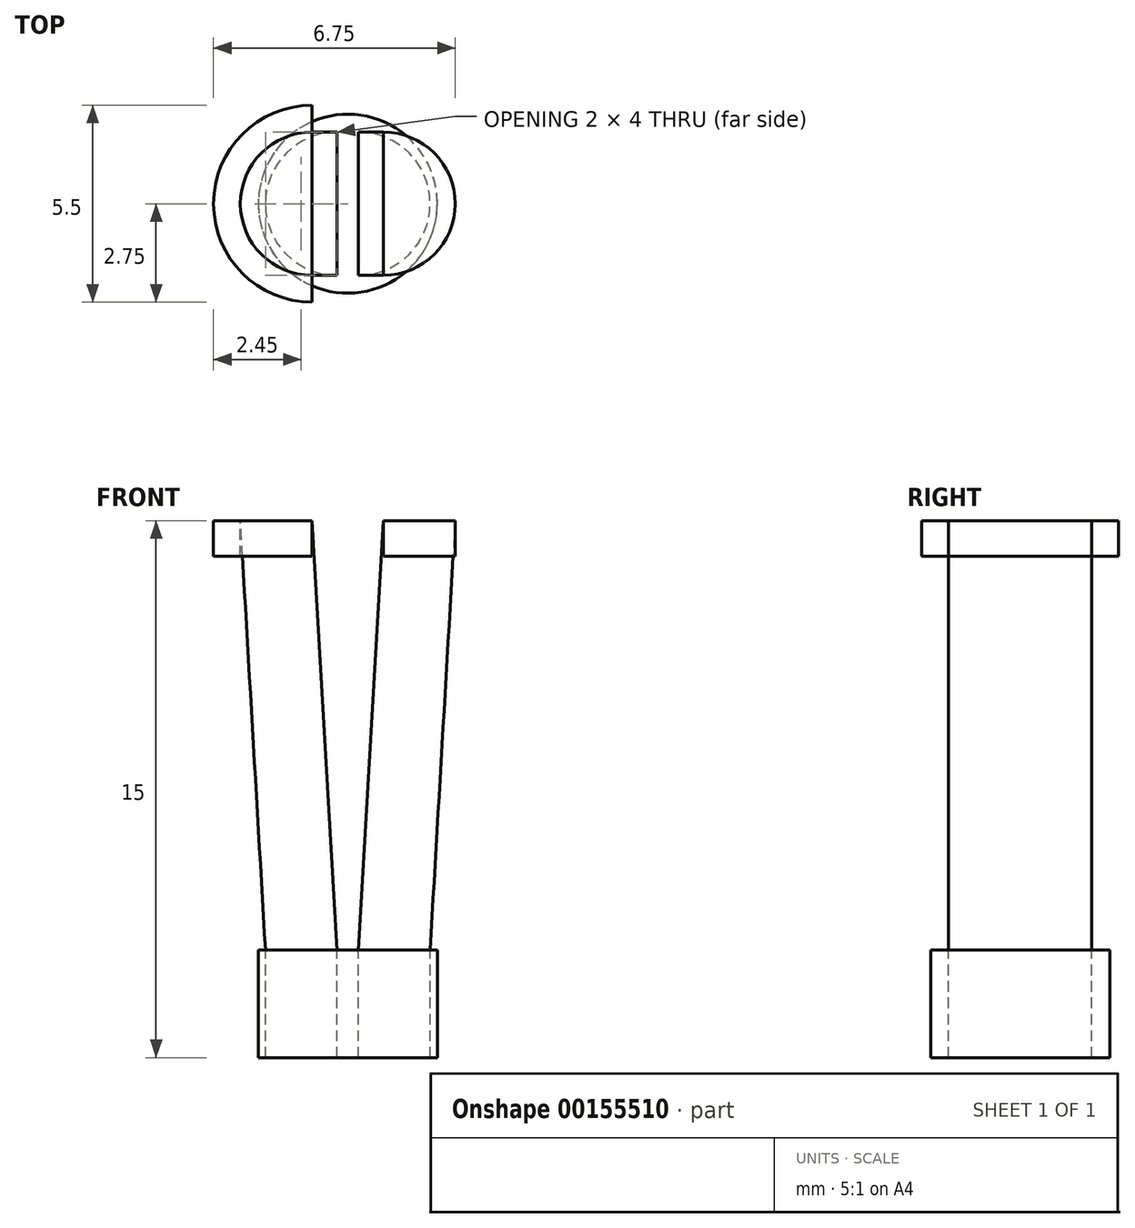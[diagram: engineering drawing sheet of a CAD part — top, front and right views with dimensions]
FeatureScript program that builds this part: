
annotation { "Feature Type Name" : "Feature", "Feature Type Description" : "" }
export const myFeature = defineFeature(function(context is Context, id is Id, definition is map)
    precondition{}
    {
        {
            var Q0;
            Q0=qCreatedBy(makeId("Top.planeOp"),FACE);
            cPlane(context, id + "F0", {"entities" : qUnion([Q0]), "cplaneType" : CPlaneType.OFFSET, "offset" : 6 * mm, "width" : 150 * mm, "height" : 150 * mm});
        }
        {
            var Q0;
            Q0=qCreatedBy(makeId("Top.planeOp"),FACE);
            cPlane(context, id + "F1", {"entities" : qUnion([Q0]), "cplaneType" : CPlaneType.OFFSET, "offset" : 6 * mm, "oppositeDirection" : true, "width" : 150 * mm, "height" : 150 * mm});
        }
        {
            var Q0;
            Q0=qCreatedBy(id+"F1.planeOp",FACE);
            var sketch = newSketch(context, id + "F2", { "sketchPlane" : qUnion([Q0])});
            skArc(sketch, "E0", {"start": v(-0.3, 2) * mm, "mid": v(-2.3, 0) * mm, "end": v(-0.3, -2) * mm});
            skLineSegment(sketch, "E1", {"start": v(-0.3, 2) * mm, "end": v(-0.3, -2) * mm});
            skLineSegment(sketch, "E2.MirrorCS", {"start": v(0.3, 2) * mm, "end": v(0.3, -2) * mm});
            skArc(sketch, "E3.MirrorCS", {"start": v(0.3, 2) * mm, "mid": v(2.3, 0) * mm, "end": v(0.3, -2) * mm});
            skSolve(sketch);
        }
        {
            var Q0;
            Q0=qCreatedBy(id+"F0.planeOp",FACE);
            var sketch = newSketch(context, id + "F3", { "sketchPlane" : qUnion([Q0])});
            skLineSegment(sketch, "E4.0", {"start": v(-0.3, 2) * mm, "end": v(-0.3, -2) * mm});
            skLineSegment(sketch, "E5.0", {"start": v(0.3, 2) * mm, "end": v(0.3, -2) * mm});
            skArc(sketch, "E6", {"start": v(-1, 2) * mm, "mid": v(-3, 0) * mm, "end": v(-1, -2) * mm});
            skLineSegment(sketch, "E7", {"start": v(-1, 2) * mm, "end": v(-1, -2) * mm});
            skLineSegment(sketch, "E8.MirrorCS", {"start": v(1, 2) * mm, "end": v(1, -2) * mm});
            skArc(sketch, "E9.MirrorCS", {"start": v(1, 2) * mm, "mid": v(3, 0) * mm, "end": v(1, -2) * mm});
            skArc(sketch, "E10.0", {"start": v(-1, 2.75) * mm, "mid": v(-3.75, 0) * mm, "end": v(-1, -2.75) * mm});
            skLineSegment(sketch, "E11", {"start": v(-1, 2.75) * mm, "end": v(-1, 2) * mm});
            skLineSegment(sketch, "E12", {"start": v(-1, -2.75) * mm, "end": v(-1, -2) * mm});
            skLineSegment(sketch, "E13.MirrorCS", {"start": v(1, 2.75) * mm, "end": v(1, 2) * mm});
            skArc(sketch, "E14.MirrorCS", {"start": v(1, 2.75) * mm, "mid": v(3.75, 0) * mm, "end": v(1, -2.75) * mm});
            skLineSegment(sketch, "E15.MirrorCS", {"start": v(1, -2.75) * mm, "end": v(1, -2) * mm});
            skSolve(sketch);
        }
        {
            var Q0;
            Q0=makeQuery(id+"F2.imprint","IMPRINT",FACE,{"disambiguationData":[TD([[makeQuery(id+"F2.imprint","IMPRINT",EDGE,{"derivedFrom":sQuery(id+"F2.wireOp",EDGE,"E2.MirrorCS")}),1.0]])]});
            var Q1;
            Q1=makeQuery(id+"F3.imprint","IMPRINT",FACE,{"disambiguationData":[TD([[makeQuery(id+"F3.imprint","IMPRINT",EDGE,{"derivedFrom":sQuery(id+"F3.wireOp",EDGE,"E8.MirrorCS")}),1.0]])]});
            loft(context, id + "F4", {"sheetProfilesArray" : [{ "sheetProfileEntities" : qUnion([Q0]) }, { "sheetProfileEntities" : qUnion([Q1]) }]});
        }
        {
            var Q0;
            Q0=makeQuery(id+"F3.imprint","IMPRINT",FACE,{"disambiguationData":[TD([[makeQuery(id+"F3.imprint","IMPRINT",EDGE,{"derivedFrom":sQuery(id+"F3.wireOp",EDGE,"E6")}),1.0]])]});
            var Q1;
            Q1=makeQuery(id+"F2.imprint","IMPRINT",FACE,{"disambiguationData":[TD([[makeQuery(id+"F2.imprint","IMPRINT",EDGE,{"derivedFrom":sQuery(id+"F2.wireOp",EDGE,"E0")}),1.0]])]});
            loft(context, id + "F5", {"sheetProfilesArray" : [{ "sheetProfileEntities" : qUnion([Q0]) }, { "sheetProfileEntities" : qUnion([Q1]) }]});
        }
        {
            var Q0;
            Q0=makeQuery(id+"F2.imprint","IMPRINT",FACE,{"disambiguationData":[TD([[makeQuery(id+"F2.imprint","IMPRINT",EDGE,{"derivedFrom":sQuery(id+"F2.wireOp",EDGE,"E0")}),1.0]])]});
            var sketch = newSketch(context, id + "F6", { "sketchPlane" : qUnion([Q0])});
            skCircle(sketch, "E16", {"center": v(0, 0) * mm, "radius": 2.5 * mm});
            skCircle(sketch, "E17.0", {"center": v(0, 0) * mm, "radius": 4.5 * mm});
            skSolve(sketch);
        }
        {
            var Q0;
            Q0=makeQuery(id+"F6.imprint","IMPRINT",FACE,{"disambiguationData":[TD([[makeQuery(id+"F6.imprint","IMPRINT",EDGE,{"derivedFrom":sQuery(id+"F6.wireOp",EDGE,"E16")}),1.0]])]});
            var Q1;
            Q1=makeQuery(id+"F2.imprint","IMPRINT",FACE,{"disambiguationData":[TD([[makeQuery(id+"F2.imprint","IMPRINT",EDGE,{"derivedFrom":sQuery(id+"F2.wireOp",EDGE,"E0")}),1.0]])]});
            var Q2;
            Q2=makeQuery(id+"F2.imprint","IMPRINT",FACE,{"disambiguationData":[TD([[makeQuery(id+"F2.imprint","IMPRINT",EDGE,{"derivedFrom":sQuery(id+"F2.wireOp",EDGE,"E2.MirrorCS")}),1.0]])]});
            extrude(context, id + "F7", {"entities" : qUnion([Q0, Q1, Q2]), "oppositeDirection" : true, "depth" : 3 * mm});
        }
        {
            var Q0;
            Q0=makeQuery(id+"F3.imprint","IMPRINT",FACE,{"disambiguationData":[TD([[makeQuery(id+"F3.imprint","IMPRINT",EDGE,{"derivedFrom":sQuery(id+"F3.wireOp",EDGE,"E6")}),-1.0]])]});
            var Q1;
            Q1=makeQuery(id+"F3.imprint","IMPRINT",FACE,{"disambiguationData":[TD([[makeQuery(id+"F3.imprint","IMPRINT",EDGE,{"derivedFrom":sQuery(id+"F3.wireOp",EDGE,"E9.MirrorCS")}),1.0]])]});
            extrude(context, id + "F8", {"entities" : qUnion([Q0, Q1]), "oppositeDirection" : true, "depth" : 1 * mm});
        }
    });
